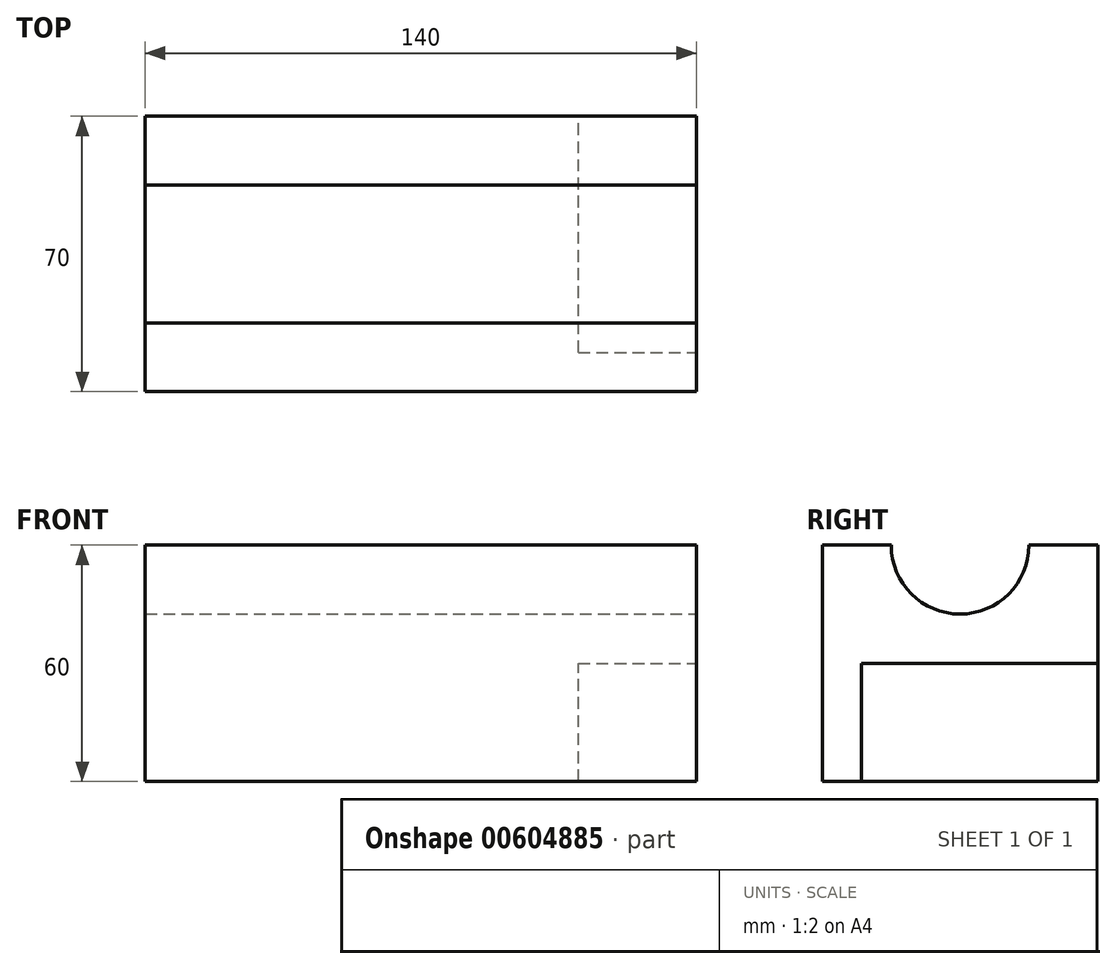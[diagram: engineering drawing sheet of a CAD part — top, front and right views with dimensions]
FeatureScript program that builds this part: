
annotation { "Feature Type Name" : "Feature", "Feature Type Description" : "" }
export const myFeature = defineFeature(function(context is Context, id is Id, definition is map)
    precondition{}
    {
        {
            var Q0;
            Q0=qCreatedBy(makeId("Top.planeOp"),FACE);
            var sketch = newSketch(context, id + "F0", { "sketchPlane" : qUnion([Q0])});
            skLineSegment(sketch, "E0", {"start": v(-72.24, 0) * mm, "end": v(67.76, 0) * mm});
            skLineSegment(sketch, "E1", {"start": v(67.76, 0) * mm, "end": v(67.76, 70) * mm});
            skLineSegment(sketch, "E2", {"start": v(67.76, 70) * mm, "end": v(-72.24, 70) * mm});
            skLineSegment(sketch, "E3", {"start": v(-72.24, 70) * mm, "end": v(-72.24, 0) * mm});
            skSolve(sketch);
        }
        {
            var Q0;
            Q0=makeQuery(id+"F0.imprint","IMPRINT",FACE,{"disambiguationData":[TD([[makeQuery(id+"F0.imprint","IMPRINT",EDGE,{"derivedFrom":sQuery(id+"F0.wireOp",EDGE,"E0")}),1.0]])]});
            extrude(context, id + "F1", {"entities" : qUnion([Q0]), "oppositeDirection" : true, "depth" : 60 * mm, "offsetDistance" : 25 * mm});
        }
        {
            var Q0;
            Q0=makeQuery(id+"F1.opExtrude","SWEPT_FACE",FACE,{"disambiguationData":[OSD([sQuery(id+"F0.wireOp",EDGE,"E1")])]});
            var sketch = newSketch(context, id + "F2", { "sketchPlane" : qUnion([Q0])});
            skCircle(sketch, "E4", {"center": v(35, 0) * mm, "radius": 17.5 * mm});
            skSolve(sketch);
        }
        {
            var Q0;
            {var subQ0=sQuery(id+"F2.wireOp",EDGE,"E4");var subQ1=makeQuery(id+"F1.opExtrude","CAP_EDGE",EDGE,{"disambiguationData":[OSD([sQuery(id+"F0.wireOp",EDGE,"E1")])],"isStart":true});var subQ2=makeQuery(id+"F2.imprint","INTERSECT",VERTEX,{"disambiguationData":[OD(0.0)],"derivedFrom":[subQ1,subQ0]});Q0=makeQuery(id+"F2.imprint","IMPRINT",FACE,{"disambiguationData":[TD([[makeQuery(id+"F2.imprint","IMPRINT",EDGE,{"disambiguationData":[TD([[subQ2,-1.0]])],"derivedFrom":subQ0}),1.0]])]});}
            extrude(context, id + "F3", {"entities" : qUnion([Q0]), "operationType" : NewBodyOperationType.REMOVE, "oppositeDirection" : true, "depth" : 142 * mm, "offsetDistance" : 25 * mm});
        }
        {
            var Q0;
            Q0=makeQuery(id+"F1.opExtrude","SWEPT_FACE",FACE,{"disambiguationData":[OSD([sQuery(id+"F0.wireOp",EDGE,"E1")])]});
            var sketch = newSketch(context, id + "F4", { "sketchPlane" : qUnion([Q0])});
            skLineSegment(sketch, "E5", {"start": v(70, -60) * mm, "end": v(70, -30) * mm});
            skLineSegment(sketch, "E6", {"start": v(70, -30) * mm, "end": v(10, -30) * mm});
            skLineSegment(sketch, "E7", {"start": v(10, -30) * mm, "end": v(10, -60) * mm});
            skLineSegment(sketch, "E8", {"start": v(70, -60) * mm, "end": v(10, -60) * mm});
            skSolve(sketch);
        }
        {
            var Q0;
            Q0=makeQuery(id+"F4.imprint","IMPRINT",FACE,{"disambiguationData":[TD([[makeQuery(id+"F4.imprint","IMPRINT",EDGE,{"derivedFrom":sQuery(id+"F4.wireOp",EDGE,"E5")}),1.0]])]});
            extrude(context, id + "F5", {"entities" : qUnion([Q0]), "operationType" : NewBodyOperationType.REMOVE, "oppositeDirection" : true, "depth" : 30 * mm, "offsetDistance" : 25 * mm});
        }
    });
